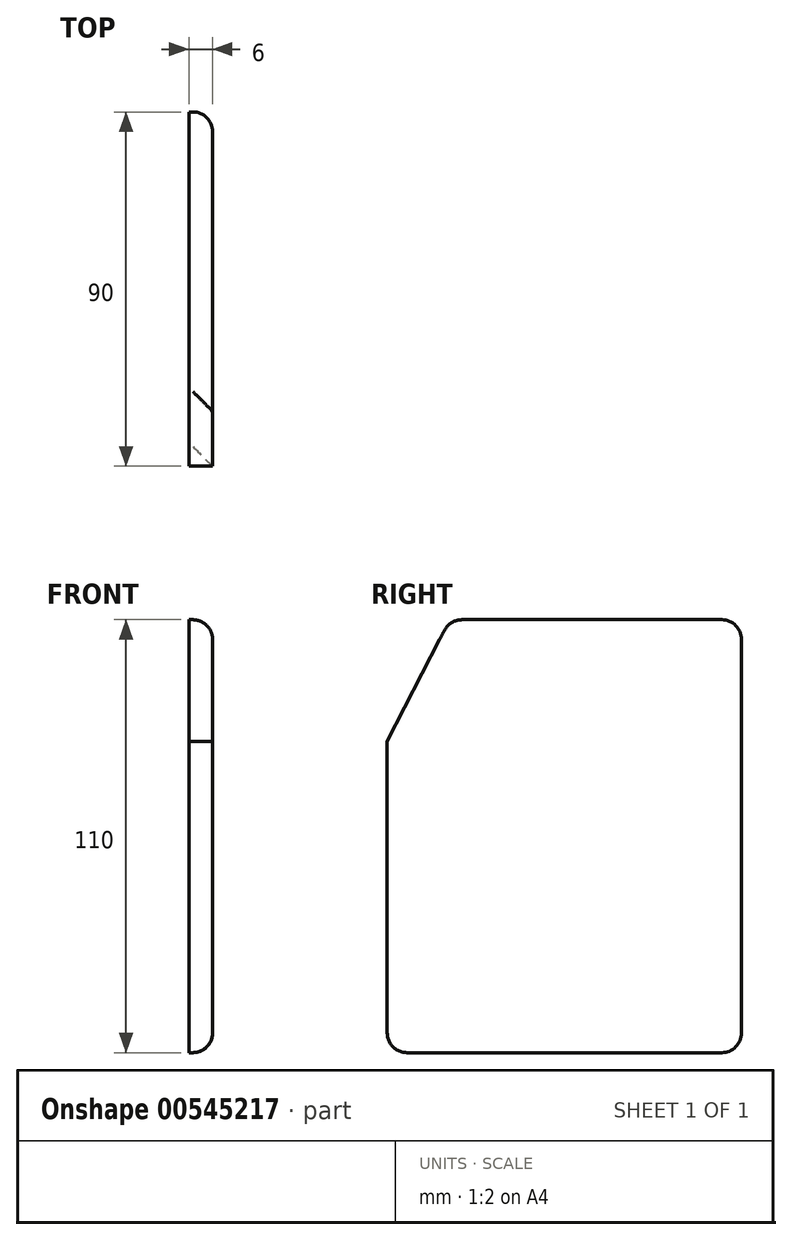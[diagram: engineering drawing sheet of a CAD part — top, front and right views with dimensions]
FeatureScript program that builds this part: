
annotation { "Feature Type Name" : "Feature", "Feature Type Description" : "" }
export const myFeature = defineFeature(function(context is Context, id is Id, definition is map)
    precondition{}
    {
        {
            var Q0;
            Q0=qCreatedBy(makeId("Right.planeOp"),FACE);
            var sketch = newSketch(context, id + "F0", { "sketchPlane" : qUnion([Q0])});
            skLineSegment(sketch, "E0.bottom", {"start": v(65.11, 42.27) * mm, "end": v(-8.97, 42.27) * mm});
            skLineSegment(sketch, "E0.top", {"start": v(65.11, -67.73) * mm, "end": v(-24.89, -67.73) * mm});
            skLineSegment(sketch, "E0.left", {"start": v(65.11, 42.27) * mm, "end": v(65.11, -67.73) * mm});
            skLineSegment(sketch, "E0.right", {"start": v(-24.89, 11.37) * mm, "end": v(-24.89, -67.73) * mm});
            skPoint(sketch, "E0.middle", {"position": v(20.11, -12.73) * mm});
            skLineSegment(sketch, "E1", {"start": v(-24.89, 11.37) * mm, "end": v(-8.97, 42.27) * mm});
            skPoint(sketch, "E2.orphan", {"position": v(-24.89, 42.27) * mm});
            skLineSegment(sketch, "E3", {"start": v(-24.89, 11.37) * mm, "end": v(-24.89, 11.37) * mm});
            skSolve(sketch);
        }
        {
            var Q0;
            Q0 = qSketchRegion(id + "F0", true);
            extrude(context, id + "F1", {"entities" : qUnion([Q0]), "depth" : 6 * mm, "offsetDistance" : 25 * mm});
        }
        {
            var Q0;
            Q0=makeQuery(id+"F1.opExtrude","CAP_EDGE",EDGE,{"disambiguationData":[OSD([sQuery(id+"F0.wireOp",EDGE,"E0.left")])],"isStart":false});
            var Q1;
            Q1=makeQuery(id+"F1.opExtrude","CAP_EDGE",EDGE,{"disambiguationData":[OSD([sQuery(id+"F0.wireOp",EDGE,"E0.bottom")])],"isStart":false});
            var Q2;
            Q2=makeQuery(id+"F1.opExtrude","CAP_EDGE",EDGE,{"disambiguationData":[OSD([sQuery(id+"F0.wireOp",EDGE,"E0.right")])],"isStart":false});
            var Q3;
            Q3=makeQuery(id+"F1.opExtrude","CAP_EDGE",EDGE,{"disambiguationData":[OSD([sQuery(id+"F0.wireOp",EDGE,"E0.top")])],"isStart":false});
            var Q4;
            Q4=makeQuery(id+"F1.opExtrude","CAP_EDGE",EDGE,{"disambiguationData":[OSD([sQuery(id+"F0.wireOp",EDGE,"E1")])],"isStart":false});
            var Q5;
            Q5=makeQuery(id+"F1.opExtrude","SWEPT_EDGE",EDGE,{"disambiguationData":[OSD([sQuery(id+"F0.wireOp",EDGE,"E1"),sQuery(id+"F0.wireOp",EDGE,"E0.right")])]});
            var Q6;
            Q6=makeQuery(id+"F1.opExtrude","SWEPT_EDGE",EDGE,{"disambiguationData":[OSD([sQuery(id+"F0.wireOp",EDGE,"E0.bottom"),sQuery(id+"F0.wireOp",EDGE,"E1")])]});
            var Q7;
            Q7=makeQuery(id+"F1.opExtrude","SWEPT_EDGE",EDGE,{"disambiguationData":[OSD([sQuery(id+"F0.wireOp",EDGE,"E0.top"),sQuery(id+"F0.wireOp",EDGE,"E0.right")])]});
            var Q8;
            Q8=makeQuery(id+"F1.opExtrude","SWEPT_EDGE",EDGE,{"disambiguationData":[OSD([sQuery(id+"F0.wireOp",EDGE,"E0.bottom"),sQuery(id+"F0.wireOp",EDGE,"E0.left")])]});
            var Q9;
            Q9=makeQuery(id+"F1.opExtrude","SWEPT_EDGE",EDGE,{"disambiguationData":[OSD([sQuery(id+"F0.wireOp",EDGE,"E0.top"),sQuery(id+"F0.wireOp",EDGE,"E0.left")])]});
            fillet(context, id + "F2", {"entities" : qUnion([Q0, Q1, Q2, Q3, Q4, Q5, Q6, Q7, Q8, Q9]), "radius" : 5 * mm, "allowEdgeOverflow" : false});
        }
    });
